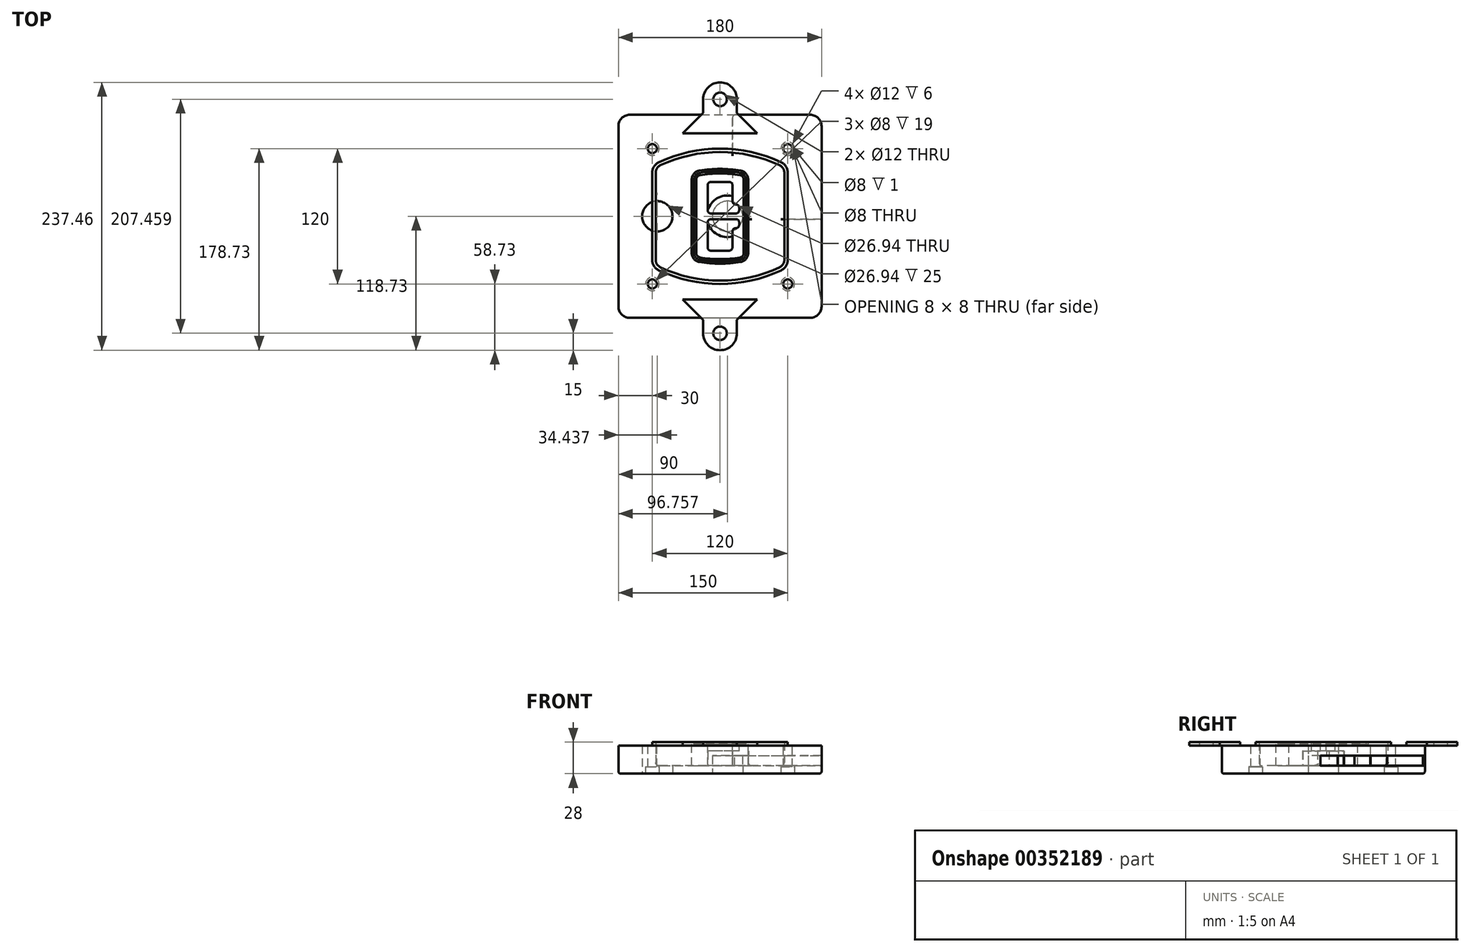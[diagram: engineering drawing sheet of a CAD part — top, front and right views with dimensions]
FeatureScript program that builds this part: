
annotation { "Feature Type Name" : "Feature", "Feature Type Description" : "" }
export const myFeature = defineFeature(function(context is Context, id is Id, definition is map)
    precondition{}
    {
        {
            var Q0;
            Q0=qCreatedBy(makeId("Top.planeOp"),FACE);
            var sketch = newSketch(context, id + "F0", { "sketchPlane" : qUnion([Q0])});
            skPoint(sketch, "E0.rect.middle", {"position": v(0, 0) * mm});
            skLineSegment(sketch, "E1.bottom", {"start": v(-80, -90) * mm, "end": v(80, -90) * mm});
            skLineSegment(sketch, "E1.top", {"start": v(-80, 90) * mm, "end": v(80, 90) * mm});
            skLineSegment(sketch, "E1.left", {"start": v(-90, -80) * mm, "end": v(-90, 80) * mm});
            skLineSegment(sketch, "E1.right", {"start": v(90, -80) * mm, "end": v(90, 80) * mm});
            skLineSegment(sketch, "E2", {"start": v(-90, 90) * mm, "end": v(90, -90) * mm, "construction": true});
            skLineSegment(sketch, "E3", {"start": v(90, 90) * mm, "end": v(-90, -90) * mm, "construction": true});
            skCircle(sketch, "E4", {"center": v(-60, 60) * mm, "radius": 4 * mm});
            skCircle(sketch, "E5", {"center": v(60, 60) * mm, "radius": 4 * mm});
            skCircle(sketch, "E6", {"center": v(60, -60) * mm, "radius": 4 * mm});
            skCircle(sketch, "E7", {"center": v(-60, -60) * mm, "radius": 4 * mm});
            skLineSegment(sketch, "E8", {"start": v(-60, 60) * mm, "end": v(60, 60) * mm, "construction": true});
            skLineSegment(sketch, "E9", {"start": v(60, 60) * mm, "end": v(60, -60) * mm, "construction": true});
            skLineSegment(sketch, "E10", {"start": v(60, -60) * mm, "end": v(-60, -60) * mm, "construction": true});
            skLineSegment(sketch, "E11", {"start": v(-60, -60) * mm, "end": v(-60, 60) * mm, "construction": true});
            skLineSegment(sketch, "E12", {"start": v(-60, 38.83) * mm, "end": v(-60, -38.83) * mm});
            skLineSegment(sketch, "E13", {"start": v(60, 38.83) * mm, "end": v(60, -38.83) * mm});
            skArc(sketch, "E14", {"start": v(54.26, 47.88) * mm, "mid": v(0, 60) * mm, "end": v(-54.26, 47.88) * mm});
            skArc(sketch, "E15", {"start": v(-54.26, -47.88) * mm, "mid": v(0, -60) * mm, "end": v(54.26, -47.88) * mm});
            skLineSegment(sketch, "E16", {"start": v(-60, 0) * mm, "end": v(60, 0) * mm, "construction": true});
            skPoint(sketch, "E17.visualSharp", {"position": v(-60, -45) * mm});
            skArc(sketch, "E17.filletArc", {"start": v(-60, -38.83) * mm, "mid": v(-58.44, -44.2) * mm, "end": v(-54.26, -47.88) * mm});
            skPoint(sketch, "E18.visualSharp", {"position": v(-60, 45) * mm});
            skArc(sketch, "E18.filletArc", {"start": v(-54.26, 47.88) * mm, "mid": v(-58.44, 44.2) * mm, "end": v(-60, 38.83) * mm});
            skPoint(sketch, "E19.visualSharp", {"position": v(60, 45) * mm});
            skArc(sketch, "E19.filletArc", {"start": v(60, 38.83) * mm, "mid": v(58.44, 44.2) * mm, "end": v(54.26, 47.88) * mm});
            skPoint(sketch, "E20.visualSharp", {"position": v(60, -45) * mm});
            skArc(sketch, "E20.filletArc", {"start": v(54.26, -47.88) * mm, "mid": v(58.44, -44.2) * mm, "end": v(60, -38.83) * mm});
            skPoint(sketch, "E21.visualSharp", {"position": v(-90, 90) * mm});
            skArc(sketch, "E21.filletArc", {"start": v(-80, 90) * mm, "mid": v(-87.07, 87.07) * mm, "end": v(-90, 80) * mm});
            skPoint(sketch, "E22.visualSharp", {"position": v(90, 90) * mm});
            skArc(sketch, "E22.filletArc", {"start": v(90, 80) * mm, "mid": v(87.07, 87.07) * mm, "end": v(80, 90) * mm});
            skPoint(sketch, "E23.visualSharp", {"position": v(90, -90) * mm});
            skArc(sketch, "E23.filletArc", {"start": v(80, -90) * mm, "mid": v(87.07, -87.07) * mm, "end": v(90, -80) * mm});
            skPoint(sketch, "E24.visualSharp", {"position": v(-90, -90) * mm});
            skArc(sketch, "E24.filletArc", {"start": v(-90, -80) * mm, "mid": v(-87.07, -87.07) * mm, "end": v(-80, -90) * mm});
            skArc(sketch, "E25.0", {"start": v(57, 38.83) * mm, "mid": v(55.9, 42.58) * mm, "end": v(52.98, 45.17) * mm});
            skLineSegment(sketch, "E25.1", {"start": v(57, 38.83) * mm, "end": v(57, -38.83) * mm});
            skArc(sketch, "E25.2", {"start": v(52.98, -45.17) * mm, "mid": v(55.9, -42.58) * mm, "end": v(57, -38.83) * mm});
            skArc(sketch, "E25.3", {"start": v(-52.98, -45.17) * mm, "mid": v(0, -57) * mm, "end": v(52.98, -45.17) * mm});
            skArc(sketch, "E25.4", {"start": v(-57, -38.83) * mm, "mid": v(-55.9, -42.58) * mm, "end": v(-52.98, -45.17) * mm});
            skArc(sketch, "E25.5", {"start": v(52.98, 45.17) * mm, "mid": v(0, 57) * mm, "end": v(-52.98, 45.17) * mm});
            skLineSegment(sketch, "E25.6", {"start": v(-57, 38.83) * mm, "end": v(-57, -38.83) * mm});
            skArc(sketch, "E25.7", {"start": v(-52.98, 45.17) * mm, "mid": v(-55.9, 42.58) * mm, "end": v(-57, 38.83) * mm});
            skArc(sketch, "E26.0", {"start": v(-55.96, 51.5) * mm, "mid": v(-61.82, 46.33) * mm, "end": v(-64, 38.83) * mm});
            skArc(sketch, "E26.1", {"start": v(55.96, 51.5) * mm, "mid": v(0, 64) * mm, "end": v(-55.96, 51.5) * mm});
            skArc(sketch, "E26.2", {"start": v(64, 38.83) * mm, "mid": v(61.82, 46.33) * mm, "end": v(55.96, 51.5) * mm});
            skLineSegment(sketch, "E26.3", {"start": v(64, 38.83) * mm, "end": v(64, -38.83) * mm});
            skArc(sketch, "E26.4", {"start": v(55.96, -51.5) * mm, "mid": v(61.82, -46.33) * mm, "end": v(64, -38.83) * mm});
            skLineSegment(sketch, "E26.5", {"start": v(-64, 38.83) * mm, "end": v(-64, -38.83) * mm});
            skArc(sketch, "E26.6", {"start": v(-55.96, -51.5) * mm, "mid": v(0, -64) * mm, "end": v(55.96, -51.5) * mm});
            skArc(sketch, "E26.7", {"start": v(-64, -38.83) * mm, "mid": v(-61.82, -46.33) * mm, "end": v(-55.96, -51.5) * mm});
            skSolve(sketch);
        }
        {
            var Q0;
            Q0=makeQuery(id+"F0.imprint","IMPRINT",FACE,{"disambiguationData":[TD([[makeQuery(id+"F0.imprint","IMPRINT",EDGE,{"derivedFrom":sQuery(id+"F0.wireOp",EDGE,"E1.bottom")}),1.0]])]});
            var Q1;
            Q1=makeQuery(id+"F0.imprint","IMPRINT",FACE,{"disambiguationData":[TD([[makeQuery(id+"F0.imprint","IMPRINT",EDGE,{"derivedFrom":sQuery(id+"F0.wireOp",EDGE,"E12")}),1.0]])]});
            var Q2;
            Q2=makeQuery(id+"F0.imprint","IMPRINT",FACE,{"disambiguationData":[TD([[makeQuery(id+"F0.imprint","IMPRINT",EDGE,{"derivedFrom":sQuery(id+"F0.wireOp",EDGE,"E25.0")}),1.0]])]});
            var Q3;
            Q3=makeQuery(id+"F0.imprint","IMPRINT",FACE,{"disambiguationData":[TD([[makeQuery(id+"F0.imprint","IMPRINT",EDGE,{"derivedFrom":sQuery(id+"F0.wireOp",EDGE,"E12")}),-1.0]])]});
            extrude(context, id + "F1", {"entities" : qUnion([Q0, Q1, Q2, Q3]), "oppositeDirection" : true, "depth" : 25 * mm});
        }
        {
            var Q0;
            Q0=makeQuery(id+"F0.imprint","IMPRINT",FACE,{"disambiguationData":[TD([[makeQuery(id+"F0.imprint","IMPRINT",EDGE,{"derivedFrom":sQuery(id+"F0.wireOp",EDGE,"E12")}),1.0]])]});
            extrude(context, id + "F2", {"entities" : qUnion([Q0]), "operationType" : NewBodyOperationType.ADD, "depth" : 3 * mm});
        }
        {
            var Q0;
            Q0=makeQuery(id+"F0.imprint","IMPRINT",FACE,{"disambiguationData":[TD([[makeQuery(id+"F0.imprint","IMPRINT",EDGE,{"derivedFrom":sQuery(id+"F0.wireOp",EDGE,"E25.0")}),1.0]])]});
            extrude(context, id + "F3", {"entities" : qUnion([Q0]), "operationType" : NewBodyOperationType.REMOVE, "oppositeDirection" : true, "depth" : 18 * mm});
        }
        {
            var Q0;
            Q0=makeQuery(id+"F2.opExtrude","CAP_FACE",FACE,{"disambiguationData":[OSD([sQuery(id+"F0.wireOp",EDGE,"E12"),sQuery(id+"F0.wireOp",EDGE,"E13"),sQuery(id+"F0.wireOp",EDGE,"E14"),sQuery(id+"F0.wireOp",EDGE,"E15"),sQuery(id+"F0.wireOp",EDGE,"E17.filletArc"),sQuery(id+"F0.wireOp",EDGE,"E18.filletArc"),sQuery(id+"F0.wireOp",EDGE,"E19.filletArc"),sQuery(id+"F0.wireOp",EDGE,"E20.filletArc"),sQuery(id+"F0.wireOp",EDGE,"E25.0"),sQuery(id+"F0.wireOp",EDGE,"E25.1"),sQuery(id+"F0.wireOp",EDGE,"E25.2"),sQuery(id+"F0.wireOp",EDGE,"E25.3"),sQuery(id+"F0.wireOp",EDGE,"E25.4"),sQuery(id+"F0.wireOp",EDGE,"E25.5"),sQuery(id+"F0.wireOp",EDGE,"E25.6"),sQuery(id+"F0.wireOp",EDGE,"E25.7")])],"isStart":false});
            var sketch = newSketch(context, id + "F4", { "sketchPlane" : qUnion([Q0])});
            skArc(sketch, "E27.0", {"start": v(-18.34, -40.45) * mm, "mid": v(0, -42) * mm, "end": v(18.34, -40.45) * mm});
            skArc(sketch, "E28.0", {"start": v(18.34, 40.45) * mm, "mid": v(0, 42) * mm, "end": v(-18.34, 40.45) * mm});
            skLineSegment(sketch, "E29", {"start": v(-25, 32.57) * mm, "end": v(-25, -32.57) * mm});
            skLineSegment(sketch, "E30", {"start": v(25, 32.57) * mm, "end": v(25, -32.57) * mm});
            skLineSegment(sketch, "E31", {"start": v(-25, 39.1) * mm, "end": v(25, 39.1) * mm, "construction": true});
            skLineSegment(sketch, "E32", {"start": v(-25, -39.1) * mm, "end": v(25, -39.1) * mm, "construction": true});
            skPoint(sketch, "E33.visualSharp", {"position": v(-25, 39.1) * mm});
            skArc(sketch, "E33.filletArc", {"start": v(-18.34, 40.45) * mm, "mid": v(-23.11, 37.73) * mm, "end": v(-25, 32.57) * mm});
            skPoint(sketch, "E34.visualSharp", {"position": v(25, 39.1) * mm});
            skArc(sketch, "E34.filletArc", {"start": v(25, 32.57) * mm, "mid": v(23.11, 37.73) * mm, "end": v(18.34, 40.45) * mm});
            skPoint(sketch, "E35.visualSharp", {"position": v(25, -39.1) * mm});
            skArc(sketch, "E35.filletArc", {"start": v(18.34, -40.45) * mm, "mid": v(23.11, -37.73) * mm, "end": v(25, -32.57) * mm});
            skPoint(sketch, "E36.visualSharp", {"position": v(-25, -39.1) * mm});
            skArc(sketch, "E36.filletArc", {"start": v(-25, -32.57) * mm, "mid": v(-23.11, -37.73) * mm, "end": v(-18.34, -40.45) * mm});
            skArc(sketch, "E37.0", {"start": v(52.98, 45.17) * mm, "mid": v(0, 57) * mm, "end": v(-52.98, 45.17) * mm});
            skArc(sketch, "E37.1", {"start": v(-52.98, 45.17) * mm, "mid": v(-55.9, 42.58) * mm, "end": v(-57, 38.83) * mm});
            skLineSegment(sketch, "E37.2", {"start": v(-57, 38.83) * mm, "end": v(-57, -38.83) * mm});
            skArc(sketch, "E37.3", {"start": v(-57, -38.83) * mm, "mid": v(-55.9, -42.58) * mm, "end": v(-52.98, -45.17) * mm});
            skArc(sketch, "E37.4", {"start": v(-52.98, -45.17) * mm, "mid": v(0, -57) * mm, "end": v(52.98, -45.17) * mm});
            skArc(sketch, "E37.5", {"start": v(52.98, -45.17) * mm, "mid": v(55.9, -42.58) * mm, "end": v(57, -38.83) * mm});
            skLineSegment(sketch, "E37.6", {"start": v(57, 38.83) * mm, "end": v(57, -38.83) * mm});
            skArc(sketch, "E37.7", {"start": v(57, 38.83) * mm, "mid": v(55.9, 42.58) * mm, "end": v(52.98, 45.17) * mm});
            skLineSegment(sketch, "E38.0", {"start": v(23, 32.57) * mm, "end": v(23, -32.57) * mm});
            skArc(sketch, "E38.1", {"start": v(18, -38.48) * mm, "mid": v(21.58, -36.44) * mm, "end": v(23, -32.57) * mm});
            skArc(sketch, "E38.2", {"start": v(-18, -38.48) * mm, "mid": v(0, -40) * mm, "end": v(18, -38.48) * mm});
            skArc(sketch, "E38.3", {"start": v(-23, -32.57) * mm, "mid": v(-21.58, -36.44) * mm, "end": v(-18, -38.48) * mm});
            skLineSegment(sketch, "E38.4", {"start": v(-23, 32.57) * mm, "end": v(-23, -32.57) * mm});
            skArc(sketch, "E38.5", {"start": v(23, 32.57) * mm, "mid": v(21.58, 36.44) * mm, "end": v(18, 38.48) * mm});
            skArc(sketch, "E38.6", {"start": v(-18, 38.48) * mm, "mid": v(-21.58, 36.44) * mm, "end": v(-23, 32.57) * mm});
            skArc(sketch, "E38.7", {"start": v(18, 38.48) * mm, "mid": v(0, 40) * mm, "end": v(-18, 38.48) * mm});
            skArc(sketch, "E39.0", {"start": v(21, 32.57) * mm, "mid": v(20.06, 35.15) * mm, "end": v(17.67, 36.5) * mm});
            skLineSegment(sketch, "E39.1", {"start": v(21, 32.57) * mm, "end": v(21, -32.57) * mm});
            skArc(sketch, "E39.2", {"start": v(17.67, -36.5) * mm, "mid": v(20.06, -35.15) * mm, "end": v(21, -32.57) * mm});
            skArc(sketch, "E39.3", {"start": v(-17.67, -36.5) * mm, "mid": v(0, -38) * mm, "end": v(17.67, -36.5) * mm});
            skArc(sketch, "E39.4", {"start": v(-21, -32.57) * mm, "mid": v(-20.06, -35.15) * mm, "end": v(-17.67, -36.5) * mm});
            skArc(sketch, "E39.5", {"start": v(17.67, 36.5) * mm, "mid": v(0, 38) * mm, "end": v(-17.67, 36.5) * mm});
            skLineSegment(sketch, "E39.6", {"start": v(-21, 32.57) * mm, "end": v(-21, -32.57) * mm});
            skArc(sketch, "E39.7", {"start": v(-17.67, 36.5) * mm, "mid": v(-20.06, 35.15) * mm, "end": v(-21, 32.57) * mm});
            skLineSegment(sketch, "E40", {"start": v(-25, 0) * mm, "end": v(25, 0) * mm, "construction": true});
            skLineSegment(sketch, "E41", {"start": v(-11, 5.5) * mm, "end": v(-11, 27.5) * mm});
            skLineSegment(sketch, "E42", {"start": v(-8, 30.5) * mm, "end": v(8, 30.5) * mm});
            skLineSegment(sketch, "E43", {"start": v(11, 27.5) * mm, "end": v(11, 13.5) * mm});
            skLineSegment(sketch, "E44", {"start": v(14, 10.5) * mm, "end": v(14, 10.5) * mm});
            skLineSegment(sketch, "E45", {"start": v(17, 7.5) * mm, "end": v(17, 5.5) * mm});
            skLineSegment(sketch, "E46", {"start": v(14, 2.5) * mm, "end": v(-8, 2.5) * mm});
            skPoint(sketch, "E47.visualSharp", {"position": v(-11, 30.5) * mm});
            skArc(sketch, "E47.filletArc", {"start": v(-8, 30.5) * mm, "mid": v(-10.12, 29.62) * mm, "end": v(-11, 27.5) * mm});
            skPoint(sketch, "E48.visualSharp", {"position": v(11, 30.5) * mm});
            skArc(sketch, "E48.filletArc", {"start": v(11, 27.5) * mm, "mid": v(10.12, 29.62) * mm, "end": v(8, 30.5) * mm});
            skPoint(sketch, "E49.visualSharp", {"position": v(11, 10.5) * mm});
            skArc(sketch, "E49.filletArc", {"start": v(11, 13.5) * mm, "mid": v(11.88, 11.38) * mm, "end": v(14, 10.5) * mm});
            skPoint(sketch, "E50.visualSharp", {"position": v(17, 10.5) * mm});
            skArc(sketch, "E50.filletArc", {"start": v(17, 7.5) * mm, "mid": v(16.12, 9.62) * mm, "end": v(14, 10.5) * mm});
            skPoint(sketch, "E51.visualSharp", {"position": v(17, 2.5) * mm});
            skArc(sketch, "E51.filletArc", {"start": v(14, 2.5) * mm, "mid": v(16.12, 3.38) * mm, "end": v(17, 5.5) * mm});
            skPoint(sketch, "E52.visualSharp", {"position": v(-11, 2.5) * mm});
            skArc(sketch, "E52.filletArc", {"start": v(-11, 5.5) * mm, "mid": v(-10.12, 3.38) * mm, "end": v(-8, 2.5) * mm});
            skLineSegment(sketch, "E53.0.MirrorCS", {"start": v(14, -2.5) * mm, "end": v(-8, -2.5) * mm});
            skArc(sketch, "E54.0.MirrorCS", {"start": v(-11, -5.5) * mm, "mid": v(-10.12, -3.38) * mm, "end": v(-8, -2.5) * mm});
            skLineSegment(sketch, "E55.0.MirrorCS", {"start": v(-11, -5.5) * mm, "end": v(-11, -27.5) * mm});
            skArc(sketch, "E56.0.MirrorCS", {"start": v(-8, -30.5) * mm, "mid": v(-10.12, -29.62) * mm, "end": v(-11, -27.5) * mm});
            skLineSegment(sketch, "E57.0.MirrorCS", {"start": v(-8, -30.5) * mm, "end": v(8, -30.5) * mm});
            skArc(sketch, "E58.0.MirrorCS", {"start": v(11, -27.5) * mm, "mid": v(10.12, -29.62) * mm, "end": v(8, -30.5) * mm});
            skLineSegment(sketch, "E59.0.MirrorCS", {"start": v(11, -27.5) * mm, "end": v(11, -13.5) * mm});
            skArc(sketch, "E60.0.MirrorCS", {"start": v(11, -13.5) * mm, "mid": v(11.88, -11.38) * mm, "end": v(14, -10.5) * mm});
            skArc(sketch, "E61.0.MirrorCS", {"start": v(17, -7.5) * mm, "mid": v(16.12, -9.62) * mm, "end": v(14, -10.5) * mm});
            skLineSegment(sketch, "E62.0.MirrorCS", {"start": v(17, -7.5) * mm, "end": v(17, -5.5) * mm});
            skArc(sketch, "E63.0.MirrorCS", {"start": v(14, -2.5) * mm, "mid": v(16.12, -3.38) * mm, "end": v(17, -5.5) * mm});
            skSolve(sketch);
        }
        {
            var Q0;
            Q0=makeQuery(id+"F4.imprint","IMPRINT",FACE,{"disambiguationData":[TD([[makeQuery(id+"F4.imprint","IMPRINT",EDGE,{"derivedFrom":sQuery(id+"F4.wireOp",EDGE,"E27.0")}),1.0]])]});
            var Q1;
            Q1=makeQuery(id+"F4.imprint","IMPRINT",FACE,{"disambiguationData":[TD([[makeQuery(id+"F4.imprint","IMPRINT",EDGE,{"derivedFrom":sQuery(id+"F4.wireOp",EDGE,"E38.0")}),-1.0]])]});
            var Q2;
            Q2=makeQuery(id+"F4.imprint","IMPRINT",FACE,{"disambiguationData":[TD([[makeQuery(id+"F4.imprint","IMPRINT",EDGE,{"derivedFrom":sQuery(id+"F4.wireOp",EDGE,"E39.0")}),1.0]])]});
            extrude(context, id + "F5", {"entities" : qUnion([Q0, Q1, Q2]), "operationType" : NewBodyOperationType.ADD, "endBound" : BoundingType.UP_TO_NEXT, "oppositeDirection" : true, "depth" : 25 * mm});
        }
        {
            var Q0;
            Q0=makeQuery(id+"F4.imprint","IMPRINT",FACE,{"disambiguationData":[TD([[makeQuery(id+"F4.imprint","IMPRINT",EDGE,{"derivedFrom":sQuery(id+"F4.wireOp",EDGE,"E38.0")}),-1.0]])]});
            extrude(context, id + "F6", {"entities" : qUnion([Q0]), "operationType" : NewBodyOperationType.REMOVE, "oppositeDirection" : true, "depth" : 2 * mm});
        }
        {
            var Q0;
            Q0=makeQuery(id+"F1.opExtrude","CAP_FACE",FACE,{"disambiguationData":[OSD([sQuery(id+"F0.wireOp",EDGE,"E1.bottom"),sQuery(id+"F0.wireOp",EDGE,"E1.top"),sQuery(id+"F0.wireOp",EDGE,"E1.left"),sQuery(id+"F0.wireOp",EDGE,"E1.right"),sQuery(id+"F0.wireOp",EDGE,"E4"),sQuery(id+"F0.wireOp",EDGE,"E5"),sQuery(id+"F0.wireOp",EDGE,"E6"),sQuery(id+"F0.wireOp",EDGE,"E7"),sQuery(id+"F0.wireOp",EDGE,"E21.filletArc"),sQuery(id+"F0.wireOp",EDGE,"E22.filletArc"),sQuery(id+"F0.wireOp",EDGE,"E23.filletArc"),sQuery(id+"F0.wireOp",EDGE,"E24.filletArc")])],"isStart":false});
            var sketch = newSketch(context, id + "F7", { "sketchPlane" : qUnion([Q0])});
            skCircle(sketch, "E64", {"center": v(6.76, 0) * mm, "radius": 13.47 * mm});
            skCircle(sketch, "E65", {"center": v(-55.56, 0) * mm, "radius": 13.47 * mm});
            skLineSegment(sketch, "E66", {"start": v(90, 0) * mm, "end": v(-90, 0) * mm});
            skCircle(sketch, "E67", {"center": v(6.76, 0) * mm, "radius": 18.47 * mm});
            skCircle(sketch, "E68", {"center": v(60, -60) * mm, "radius": 6 * mm});
            skCircle(sketch, "E69", {"center": v(-60, -60) * mm, "radius": 6 * mm});
            skCircle(sketch, "E70", {"center": v(-60, 60) * mm, "radius": 6 * mm});
            skCircle(sketch, "E71", {"center": v(60, 60) * mm, "radius": 6 * mm});
            skSolve(sketch);
        }
        {
            var Q0;
            {var subQ1=sQuery(id+"F7.wireOp",EDGE,"E66");var subQ4=sQuery(id+"F7.wireOp",EDGE,"E64");var subQ6=makeQuery(id+"F7.imprint","INTERSECT",VERTEX,{"disambiguationData":[OD(0.0)],"derivedFrom":[subQ4,subQ1]});Q0=makeQuery(id+"F7.imprint","IMPRINT",FACE,{"disambiguationData":[TD([[makeQuery(id+"F7.imprint","IMPRINT",EDGE,{"disambiguationData":[TD([[subQ6,-1.0]])],"derivedFrom":subQ4}),-1.0]])]});}
            var Q1;
            {var subQ0=sQuery(id+"F7.wireOp",EDGE,"E66");var subQ1=sQuery(id+"F7.wireOp",EDGE,"E64");var subQ3=makeQuery(id+"F7.imprint","INTERSECT",VERTEX,{"disambiguationData":[OD(0.0)],"derivedFrom":[subQ1,subQ0]});Q1=makeQuery(id+"F7.imprint","IMPRINT",FACE,{"disambiguationData":[TD([[makeQuery(id+"F7.imprint","IMPRINT",EDGE,{"disambiguationData":[TD([[subQ3,-1.0]])],"derivedFrom":subQ1}),1.0]])]});}
            var Q2;
            {var subQ0=sQuery(id+"F7.wireOp",EDGE,"E66");var subQ1=sQuery(id+"F7.wireOp",EDGE,"E64");var subQ3=makeQuery(id+"F7.imprint","INTERSECT",VERTEX,{"disambiguationData":[OD(0.0)],"derivedFrom":[subQ1,subQ0]});Q2=makeQuery(id+"F7.imprint","IMPRINT",FACE,{"disambiguationData":[TD([[makeQuery(id+"F7.imprint","IMPRINT",EDGE,{"disambiguationData":[TD([[subQ3,1.0]])],"derivedFrom":subQ1}),1.0]])]});}
            var Q3;
            {var subQ1=sQuery(id+"F7.wireOp",EDGE,"E66");var subQ4=sQuery(id+"F7.wireOp",EDGE,"E64");var subQ6=makeQuery(id+"F7.imprint","INTERSECT",VERTEX,{"disambiguationData":[OD(0.0)],"derivedFrom":[subQ4,subQ1]});Q3=makeQuery(id+"F7.imprint","IMPRINT",FACE,{"disambiguationData":[TD([[makeQuery(id+"F7.imprint","IMPRINT",EDGE,{"disambiguationData":[TD([[subQ6,1.0]])],"derivedFrom":subQ4}),-1.0]])]});}
            extrude(context, id + "F8", {"entities" : qUnion([Q0, Q1, Q2, Q3]), "operationType" : NewBodyOperationType.ADD, "oppositeDirection" : true, "depth" : 20 * mm});
        }
        {
            var Q0;
            {var subQ0=sQuery(id+"F7.wireOp",EDGE,"E66");var subQ1=sQuery(id+"F7.wireOp",EDGE,"E64");var subQ3=makeQuery(id+"F7.imprint","INTERSECT",VERTEX,{"disambiguationData":[OD(0.0)],"derivedFrom":[subQ1,subQ0]});Q0=makeQuery(id+"F7.imprint","IMPRINT",FACE,{"disambiguationData":[TD([[makeQuery(id+"F7.imprint","IMPRINT",EDGE,{"disambiguationData":[TD([[subQ3,-1.0]])],"derivedFrom":subQ1}),1.0]])]});}
            var Q1;
            {var subQ0=sQuery(id+"F7.wireOp",EDGE,"E66");var subQ1=sQuery(id+"F7.wireOp",EDGE,"E64");var subQ3=makeQuery(id+"F7.imprint","INTERSECT",VERTEX,{"disambiguationData":[OD(0.0)],"derivedFrom":[subQ1,subQ0]});Q1=makeQuery(id+"F7.imprint","IMPRINT",FACE,{"disambiguationData":[TD([[makeQuery(id+"F7.imprint","IMPRINT",EDGE,{"disambiguationData":[TD([[subQ3,1.0]])],"derivedFrom":subQ1}),1.0]])]});}
            extrude(context, id + "F9", {"entities" : qUnion([Q0, Q1]), "operationType" : NewBodyOperationType.REMOVE, "oppositeDirection" : true, "depth" : 16 * mm});
        }
        {
            var Q0;
            {var subQ0=sQuery(id+"F7.wireOp",EDGE,"E66");var subQ1=sQuery(id+"F7.wireOp",EDGE,"E65");var subQ3=makeQuery(id+"F7.imprint","INTERSECT",VERTEX,{"disambiguationData":[OD(0.0)],"derivedFrom":[subQ1,subQ0]});Q0=makeQuery(id+"F7.imprint","IMPRINT",FACE,{"disambiguationData":[TD([[makeQuery(id+"F7.imprint","IMPRINT",EDGE,{"disambiguationData":[TD([[subQ3,-1.0]])],"derivedFrom":subQ1}),1.0]])]});}
            var Q1;
            {var subQ0=sQuery(id+"F7.wireOp",EDGE,"E66");var subQ1=sQuery(id+"F7.wireOp",EDGE,"E65");var subQ3=makeQuery(id+"F7.imprint","INTERSECT",VERTEX,{"disambiguationData":[OD(0.0)],"derivedFrom":[subQ1,subQ0]});Q1=makeQuery(id+"F7.imprint","IMPRINT",FACE,{"disambiguationData":[TD([[makeQuery(id+"F7.imprint","IMPRINT",EDGE,{"disambiguationData":[TD([[subQ3,1.0]])],"derivedFrom":subQ1}),1.0]])]});}
            extrude(context, id + "F10", {"entities" : qUnion([Q0, Q1]), "operationType" : NewBodyOperationType.REMOVE, "oppositeDirection" : true, "depth" : 25 * mm});
        }
        {
            var Q0;
            Q0=makeQuery(id+"F7.imprint","IMPRINT",FACE,{"disambiguationData":[TD([[makeQuery(id+"F7.imprint","IMPRINT",EDGE,{"derivedFrom":sQuery(id+"F7.wireOp",EDGE,"E68")}),1.0]])]});
            var Q1;
            Q1=makeQuery(id+"F7.imprint","IMPRINT",FACE,{"disambiguationData":[TD([[makeQuery(id+"F7.imprint","IMPRINT",EDGE,{"derivedFrom":makeQuery(id+"F1.opExtrude","CAP_EDGE",EDGE,{"disambiguationData":[OSD([sQuery(id+"F0.wireOp",EDGE,"E5")])],"isStart":false})}),-1.0]])]});
            var Q2;
            Q2=makeQuery(id+"F7.imprint","IMPRINT",FACE,{"disambiguationData":[TD([[makeQuery(id+"F7.imprint","IMPRINT",EDGE,{"derivedFrom":sQuery(id+"F7.wireOp",EDGE,"E69")}),1.0]])]});
            var Q3;
            Q3=makeQuery(id+"F7.imprint","IMPRINT",FACE,{"disambiguationData":[TD([[makeQuery(id+"F7.imprint","IMPRINT",EDGE,{"derivedFrom":makeQuery(id+"F1.opExtrude","CAP_EDGE",EDGE,{"disambiguationData":[OSD([sQuery(id+"F0.wireOp",EDGE,"E4")])],"isStart":false})}),-1.0]])]});
            var Q4;
            Q4=makeQuery(id+"F7.imprint","IMPRINT",FACE,{"disambiguationData":[TD([[makeQuery(id+"F7.imprint","IMPRINT",EDGE,{"derivedFrom":sQuery(id+"F7.wireOp",EDGE,"E70")}),1.0]])]});
            var Q5;
            Q5=makeQuery(id+"F7.imprint","IMPRINT",FACE,{"disambiguationData":[TD([[makeQuery(id+"F7.imprint","IMPRINT",EDGE,{"derivedFrom":makeQuery(id+"F1.opExtrude","CAP_EDGE",EDGE,{"disambiguationData":[OSD([sQuery(id+"F0.wireOp",EDGE,"E7")])],"isStart":false})}),-1.0]])]});
            var Q6;
            Q6=makeQuery(id+"F7.imprint","IMPRINT",FACE,{"disambiguationData":[TD([[makeQuery(id+"F7.imprint","IMPRINT",EDGE,{"derivedFrom":sQuery(id+"F7.wireOp",EDGE,"E71")}),1.0]])]});
            var Q7;
            Q7=makeQuery(id+"F7.imprint","IMPRINT",FACE,{"disambiguationData":[TD([[makeQuery(id+"F7.imprint","IMPRINT",EDGE,{"derivedFrom":makeQuery(id+"F1.opExtrude","CAP_EDGE",EDGE,{"disambiguationData":[OSD([sQuery(id+"F0.wireOp",EDGE,"E6")])],"isStart":false})}),-1.0]])]});
            extrude(context, id + "F11", {"entities" : qUnion([Q0, Q1, Q2, Q3, Q4, Q5, Q6, Q7]), "operationType" : NewBodyOperationType.REMOVE, "oppositeDirection" : true, "depth" : 6 * mm});
        }
        {
            var Q0;
            Q0=makeQuery(id+"F9.boolean.opBoolean","COPY",FACE,{"derivedFrom":makeQuery(id+"F9.opExtrude","CAP_FACE",FACE,{"disambiguationData":[OSD([sQuery(id+"F7.wireOp",EDGE,"E64")])],"isStart":false})});
            var sketch = newSketch(context, id + "F12", { "sketchPlane" : qUnion([Q0])});
            skArc(sketch, "E72.0", {"start": v(11, -88.19) * mm, "mid": v(97.1, -83.6) * mm, "end": v(92.5, 2.5) * mm});
            skLineSegment(sketch, "E72.1", {"start": v(11, -17.97) * mm, "end": v(11, -17.97) * mm});
            skLineSegment(sketch, "E73", {"start": v(92.5, -105.13) * mm, "end": v(102.3, -105.13) * mm});
            skLineSegment(sketch, "E74.0", {"start": v(92.5, 2.5) * mm, "end": v(14, 2.5) * mm});
            skArc(sketch, "E74.1", {"start": v(14, 2.5) * mm, "mid": v(16.12, 3.38) * mm, "end": v(17, 5.5) * mm});
            skLineSegment(sketch, "E74.2", {"start": v(17, 7.5) * mm, "end": v(17, 5.5) * mm});
            skArc(sketch, "E74.3", {"start": v(17, 7.5) * mm, "mid": v(16.12, 9.62) * mm, "end": v(14, 10.5) * mm});
            skArc(sketch, "E74.4", {"start": v(11, 13.5) * mm, "mid": v(11.88, 11.38) * mm, "end": v(14, 10.5) * mm});
            skLineSegment(sketch, "E74.5", {"start": v(11, 13.5) * mm, "end": v(11, -88.19) * mm});
            skLineSegment(sketch, "E74.7", {"start": v(92.5, -2.5) * mm, "end": v(14, -2.5) * mm});
            skArc(sketch, "E74.8", {"start": v(14, -2.5) * mm, "mid": v(16.12, -3.38) * mm, "end": v(17, -5.5) * mm});
            skLineSegment(sketch, "E74.9", {"start": v(17, -7.5) * mm, "end": v(17, -5.5) * mm});
            skArc(sketch, "E74.10", {"start": v(17, -7.5) * mm, "mid": v(16.12, -9.62) * mm, "end": v(14, -10.5) * mm});
            skArc(sketch, "E74.11", {"start": v(11, -13.5) * mm, "mid": v(11.88, -11.38) * mm, "end": v(14, -10.5) * mm});
            skLineSegment(sketch, "E74.12", {"start": v(11, -17.97) * mm, "end": v(11, -13.5) * mm});
            skPoint(sketch, "E75.orphan", {"position": v(11, -27.5) * mm});
            skPoint(sketch, "E76.orphan", {"position": v(-8, -2.5) * mm});
            skPoint(sketch, "E77.orphan", {"position": v(-8, 2.5) * mm});
            skPoint(sketch, "E78.orphan", {"position": v(11, 27.5) * mm});
            skSolve(sketch);
        }
        {
            var Q0;
            {var subQ7=sQuery(id+"F12.wireOp",EDGE,"E72.0");var subQ14=sQuery(id+"F12.wireOp",EDGE,"E72.1");var subQ16=sQuery(id+"F12.wireOp",EDGE,"E74.1");var subQ18=sQuery(id+"F12.wireOp",EDGE,"E74.8");Q0=qUnion([makeQuery(id+"F12.imprint","IMPRINT",FACE,{"disambiguationData":[TD([[makeQuery(id+"F12.imprint","IMPRINT",EDGE,{"derivedFrom":subQ7}),1.0]])]}),makeQuery(id+"F12.imprint","IMPRINT",FACE,{"disambiguationData":[TD([[makeQuery(id+"F12.imprint","IMPRINT",EDGE,{"derivedFrom":subQ14}),1.0]])]}),makeQuery(id+"F12.imprint","IMPRINT",FACE,{"disambiguationData":[TD([[makeQuery(id+"F12.imprint","IMPRINT",EDGE,{"derivedFrom":subQ16}),1.0]])]}),makeQuery(id+"F12.imprint","IMPRINT",FACE,{"disambiguationData":[TD([[makeQuery(id+"F12.imprint","IMPRINT",EDGE,{"derivedFrom":subQ18}),-1.0]])]})]);}
            var Q1;
            Q1=makeQuery(id+"F5.boolean.opBoolean","SPLIT",FACE,{"disambiguationData":[TD([makeQuery(id+"F5.opExtrude","SWEPT_FACE",FACE,{"disambiguationData":[OSD([sQuery(id+"F4.wireOp",EDGE,"E41")])]})])],"derivedFrom":makeQuery(id+"F3.boolean.opBoolean","COPY",FACE,{"derivedFrom":makeQuery(id+"F3.opExtrude","CAP_FACE",FACE,{"disambiguationData":[OSD([sQuery(id+"F0.wireOp",EDGE,"E25.0"),sQuery(id+"F0.wireOp",EDGE,"E25.1"),sQuery(id+"F0.wireOp",EDGE,"E25.2"),sQuery(id+"F0.wireOp",EDGE,"E25.3"),sQuery(id+"F0.wireOp",EDGE,"E25.4"),sQuery(id+"F0.wireOp",EDGE,"E25.5"),sQuery(id+"F0.wireOp",EDGE,"E25.6"),sQuery(id+"F0.wireOp",EDGE,"E25.7")])],"isStart":false})})});
            extrude(context, id + "F13", {"entities" : qUnion([Q0]), "operationType" : NewBodyOperationType.REMOVE, "endBound" : BoundingType.UP_TO_SURFACE, "endBoundEntityFace" : qUnion([Q1]), "depth" : 25 * mm});
        }
        {
            var Q0;
            Q0=makeQuery(id+"F3.boolean.opBoolean","COPY",EDGE,{"derivedFrom":makeQuery(id+"F3.opExtrude","CAP_EDGE",EDGE,{"disambiguationData":[OSD([sQuery(id+"F0.wireOp",EDGE,"E25.6")])],"isStart":false})});
            var Q1;
            Q1=makeQuery(id+"F8.boolean.opBoolean","INTERSECT",EDGE,{"derivedFrom":[makeQuery(id+"F5.opExtrude","SWEPT_FACE",FACE,{"disambiguationData":[OSD([sQuery(id+"F4.wireOp",EDGE,"E30")])]}),makeQuery(id+"F8.opExtrude","CAP_FACE",FACE,{"disambiguationData":[OSD([sQuery(id+"F7.wireOp",EDGE,"E67")])],"isStart":false})]});
            var Q2;
            Q2=makeQuery(id+"F8.boolean.opBoolean","INTERSECT",EDGE,{"disambiguationData":[OD(1.0)],"derivedFrom":[makeQuery(id+"F5.opExtrude","SWEPT_FACE",FACE,{"disambiguationData":[OSD([sQuery(id+"F4.wireOp",EDGE,"E30")])]}),makeQuery(id+"F8.opExtrude","SWEPT_FACE",FACE,{"disambiguationData":[OSD([sQuery(id+"F7.wireOp",EDGE,"E67")])]})]});
            var Q3;
            {var subQ0=makeQuery(id+"F3.boolean.opBoolean","COPY",FACE,{"derivedFrom":makeQuery(id+"F3.opExtrude","CAP_FACE",FACE,{"disambiguationData":[OSD([sQuery(id+"F0.wireOp",EDGE,"E25.0"),sQuery(id+"F0.wireOp",EDGE,"E25.1"),sQuery(id+"F0.wireOp",EDGE,"E25.2"),sQuery(id+"F0.wireOp",EDGE,"E25.3"),sQuery(id+"F0.wireOp",EDGE,"E25.4"),sQuery(id+"F0.wireOp",EDGE,"E25.5"),sQuery(id+"F0.wireOp",EDGE,"E25.6"),sQuery(id+"F0.wireOp",EDGE,"E25.7")])],"isStart":false})});var subQ1=sQuery(id+"F4.wireOp",EDGE,"E30");Q3=makeQuery(id+"F8.boolean.opBoolean","SPLIT",EDGE,{"disambiguationData":[TD([makeQuery(id+"F5.opExtrude","SWEPT_FACE",FACE,{"disambiguationData":[OSD([sQuery(id+"F4.wireOp",EDGE,"E35.filletArc")])]})])],"derivedFrom":makeQuery(id+"F5.opExtrude","TWEAK_EDGE",EDGE,{"derivedFrom":[subQ0,makeQuery(id+"F4.imprint","IMPRINT",EDGE,{"derivedFrom":subQ1})]})});}
            var Q4;
            {var subQ0=sQuery(id+"F0.wireOp",EDGE,"E25.0");var subQ1=sQuery(id+"F0.wireOp",EDGE,"E25.1");var subQ2=sQuery(id+"F0.wireOp",EDGE,"E25.2");var subQ3=sQuery(id+"F0.wireOp",EDGE,"E25.3");var subQ4=sQuery(id+"F0.wireOp",EDGE,"E25.4");var subQ5=sQuery(id+"F0.wireOp",EDGE,"E25.5");var subQ6=sQuery(id+"F0.wireOp",EDGE,"E25.6");var subQ7=sQuery(id+"F0.wireOp",EDGE,"E25.7");Q4=makeQuery(id+"F8.boolean.opBoolean","INTERSECT",EDGE,{"derivedFrom":[makeQuery(id+"F5.boolean.opBoolean","SPLIT",FACE,{"disambiguationData":[TD([makeQuery(id+"F2.opExtrude","SWEPT_FACE",FACE,{"disambiguationData":[OSD([subQ0])]})])],"derivedFrom":makeQuery(id+"F3.boolean.opBoolean","COPY",FACE,{"derivedFrom":makeQuery(id+"F3.opExtrude","CAP_FACE",FACE,{"disambiguationData":[OSD([subQ0,subQ1,subQ2,subQ3,subQ4,subQ5,subQ6,subQ7])],"isStart":false})})}),makeQuery(id+"F8.opExtrude","SWEPT_FACE",FACE,{"disambiguationData":[OSD([sQuery(id+"F7.wireOp",EDGE,"E67")])]})]});}
            var Q5;
            Q5=makeQuery(id+"F8.boolean.opBoolean","INTERSECT",EDGE,{"disambiguationData":[OD(0.0)],"derivedFrom":[makeQuery(id+"F5.opExtrude","SWEPT_FACE",FACE,{"disambiguationData":[OSD([sQuery(id+"F4.wireOp",EDGE,"E30")])]}),makeQuery(id+"F8.opExtrude","SWEPT_FACE",FACE,{"disambiguationData":[OSD([sQuery(id+"F7.wireOp",EDGE,"E67")])]})]});
            fillet(context, id + "F14", {"entities" : qUnion([Q0, Q1, Q2, Q3, Q4, Q5]), "radius" : 3 * mm, "tangentPropagation" : true, "allowEdgeOverflow" : false});
        }
        {
            var Q0;
            Q0=makeQuery(id+"F1.opExtrude","CAP_EDGE",EDGE,{"disambiguationData":[OSD([sQuery(id+"F0.wireOp",EDGE,"E1.bottom")])],"isStart":false});
            fillet(context, id + "F15", {"entities" : qUnion([Q0]), "radius" : 2 * mm, "tangentPropagation" : true, "allowEdgeOverflow" : false});
        }
        {
            var Q0;
            Q0=qCreatedBy(makeId("Top.planeOp"),FACE);
            var sketch = newSketch(context, id + "F16", { "sketchPlane" : qUnion([Q0])});
            skLineSegment(sketch, "E79", {"start": v(-33, 73.73) * mm, "end": v(-15, 91.73) * mm});
            skLineSegment(sketch, "E80", {"start": v(-15, 91.73) * mm, "end": v(-15, 103.73) * mm});
            skLineSegment(sketch, "E81", {"start": v(-33, 73.73) * mm, "end": v(33, 73.73) * mm});
            skLineSegment(sketch, "E82", {"start": v(33, 73.73) * mm, "end": v(15, 91.73) * mm});
            skLineSegment(sketch, "E83", {"start": v(15, 91.73) * mm, "end": v(15, 103.73) * mm});
            skArc(sketch, "E84", {"start": v(15, 103.73) * mm, "mid": v(0, 118.73) * mm, "end": v(-15, 103.73) * mm});
            skCircle(sketch, "E85", {"center": v(0, 103.73) * mm, "radius": 6 * mm});
            skLineSegment(sketch, "E86", {"start": v(0, 103.73) * mm, "end": v(0, 73.73) * mm, "construction": true});
            skLineSegment(sketch, "E87", {"start": v(-74.33, 0) * mm, "end": v(73.14, 0) * mm, "construction": true});
            skArc(sketch, "E88.MirrorCS", {"start": v(15, -103.73) * mm, "mid": v(0, -118.73) * mm, "end": v(-15, -103.73) * mm});
            skCircle(sketch, "E89.MirrorC", {"center": v(0, -103.73) * mm, "radius": 6 * mm});
            skLineSegment(sketch, "E90.MirrorCS", {"start": v(0, -103.73) * mm, "end": v(0, -73.73) * mm, "construction": true});
            skLineSegment(sketch, "E91.MirrorCS", {"start": v(15, -91.73) * mm, "end": v(15, -103.73) * mm});
            skLineSegment(sketch, "E92.MirrorCS", {"start": v(-15, -91.73) * mm, "end": v(-15, -103.73) * mm});
            skLineSegment(sketch, "E93.MirrorCS", {"start": v(-33, -73.73) * mm, "end": v(-15, -91.73) * mm});
            skLineSegment(sketch, "E94.MirrorCS", {"start": v(-33, -73.73) * mm, "end": v(33, -73.73) * mm});
            skLineSegment(sketch, "E95.MirrorCS", {"start": v(33, -73.73) * mm, "end": v(15, -91.73) * mm});
            skSolve(sketch);
        }
        {
            var Q0;
            Q0 = qSketchRegion(id + "F16", true);
            var Q1;
            Q1=makeQuery(id+"F2.opExtrude","CAP_FACE",FACE,{"disambiguationData":[OSD([sQuery(id+"F0.wireOp",EDGE,"E12"),sQuery(id+"F0.wireOp",EDGE,"E13"),sQuery(id+"F0.wireOp",EDGE,"E14"),sQuery(id+"F0.wireOp",EDGE,"E15"),sQuery(id+"F0.wireOp",EDGE,"E17.filletArc"),sQuery(id+"F0.wireOp",EDGE,"E18.filletArc"),sQuery(id+"F0.wireOp",EDGE,"E19.filletArc"),sQuery(id+"F0.wireOp",EDGE,"E20.filletArc"),sQuery(id+"F0.wireOp",EDGE,"E25.0"),sQuery(id+"F0.wireOp",EDGE,"E25.1"),sQuery(id+"F0.wireOp",EDGE,"E25.2"),sQuery(id+"F0.wireOp",EDGE,"E25.3"),sQuery(id+"F0.wireOp",EDGE,"E25.4"),sQuery(id+"F0.wireOp",EDGE,"E25.5"),sQuery(id+"F0.wireOp",EDGE,"E25.6"),sQuery(id+"F0.wireOp",EDGE,"E25.7")])],"isStart":false});
            extrude(context, id + "F17", {"entities" : qUnion([Q0]), "endBound" : BoundingType.UP_TO_SURFACE, "endBoundEntityFace" : qUnion([Q1]), "depth" : 25 * mm});
        }
    });
